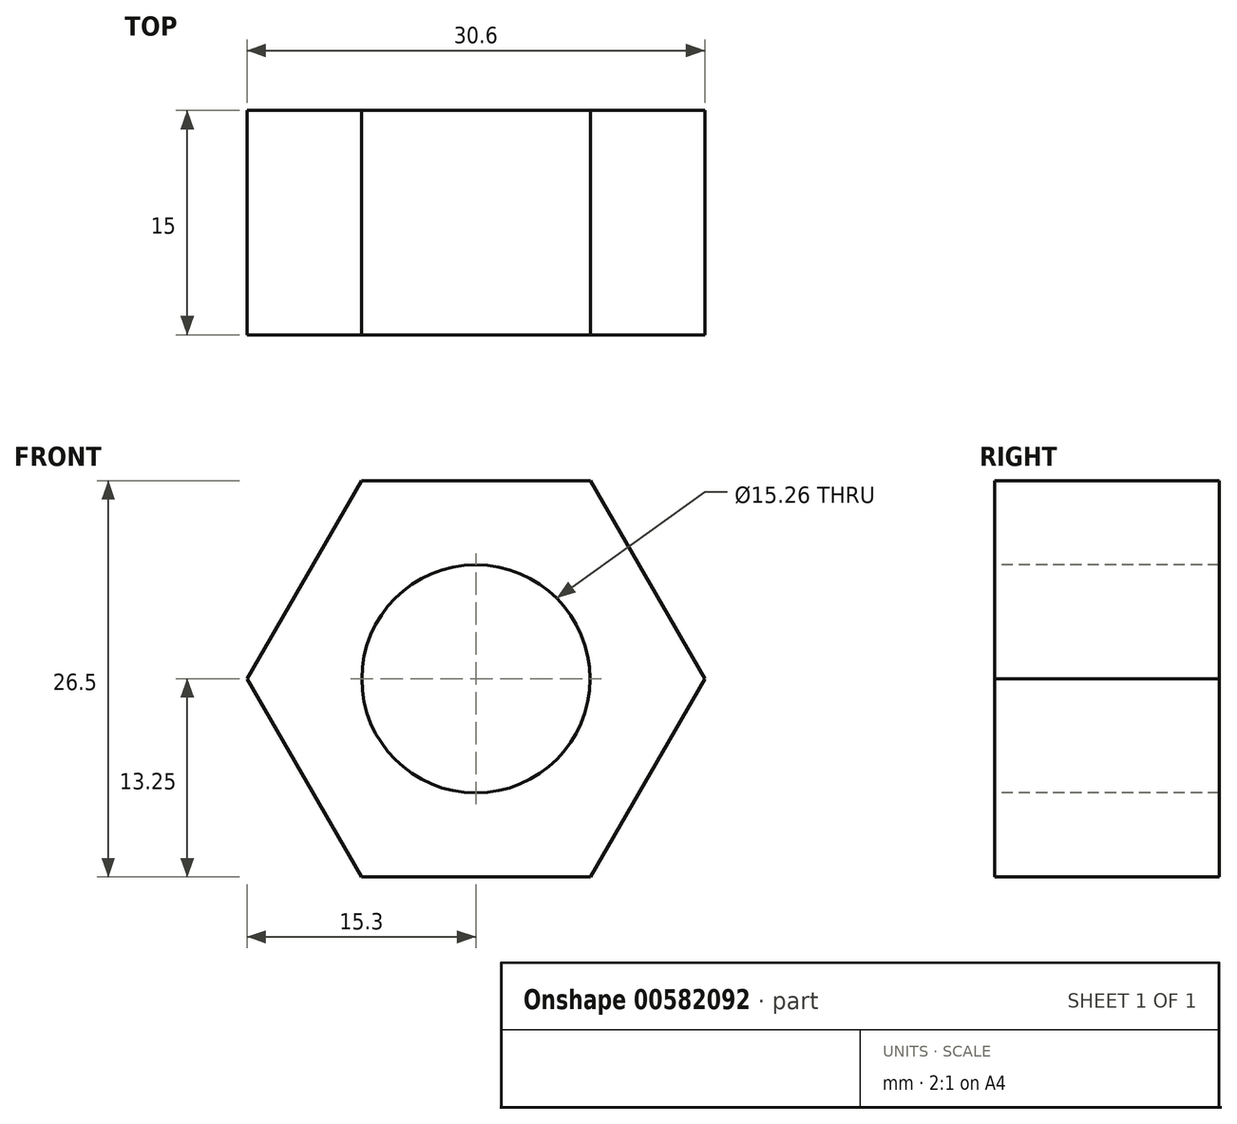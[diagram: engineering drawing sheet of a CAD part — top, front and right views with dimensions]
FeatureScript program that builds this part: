
annotation { "Feature Type Name" : "Feature", "Feature Type Description" : "" }
export const myFeature = defineFeature(function(context is Context, id is Id, definition is map)
    precondition{}
    {
        {
            var Q0;
            Q0=qCreatedBy(makeId("Front.planeOp"),FACE);
            var sketch = newSketch(context, id + "F0", { "sketchPlane" : qUnion([Q0])});
            skCircle(sketch, "E0.cCircle", {"center": v(0, 0) * mm, "radius": 13.25 * mm, "construction": true});
            skLineSegment(sketch, "E0.0", {"start": v(-15.3, 0) * mm, "end": v(-7.65, 13.25) * mm});
            skLineSegment(sketch, "E0.1", {"start": v(-7.65, 13.25) * mm, "end": v(7.65, 13.25) * mm});
            skLineSegment(sketch, "E0.2", {"start": v(7.65, 13.25) * mm, "end": v(15.3, 0) * mm});
            skLineSegment(sketch, "E0.3", {"start": v(15.3, 0) * mm, "end": v(7.65, -13.25) * mm});
            skLineSegment(sketch, "E0.4", {"start": v(7.65, -13.25) * mm, "end": v(-7.65, -13.25) * mm});
            skLineSegment(sketch, "E0.5", {"start": v(-7.65, -13.25) * mm, "end": v(-15.3, 0) * mm});
            skPoint(sketch, "E0.0.midPoint", {"position": v(-11.47, 6.63) * mm});
            skSolve(sketch);
        }
        {
            var Q0;
            Q0 = qSketchRegion(id + "F0", true);
            extrude(context, id + "F1", {"entities" : qUnion([Q0]), "depth" : 15 * mm, "offsetDistance" : 25 * mm});
        }
        {
            var Q0;
            Q0=makeQuery(id+"F1.opExtrude","CAP_FACE",FACE,{"disambiguationData":[OSD([sQuery(id+"F0.wireOp",EDGE,"E0.0"),sQuery(id+"F0.wireOp",EDGE,"E0.1"),sQuery(id+"F0.wireOp",EDGE,"E0.2"),sQuery(id+"F0.wireOp",EDGE,"E0.3"),sQuery(id+"F0.wireOp",EDGE,"E0.4"),sQuery(id+"F0.wireOp",EDGE,"E0.5")])],"isStart":false});
            var sketch = newSketch(context, id + "F2", { "sketchPlane" : qUnion([Q0])});
            skCircle(sketch, "E1", {"center": v(0, 0) * mm, "radius": 7.63 * mm});
            skSolve(sketch);
        }
        {
            var Q0;
            Q0 = qSketchRegion(id + "F2", true);
            extrude(context, id + "F3", {"entities" : qUnion([Q0]), "operationType" : NewBodyOperationType.REMOVE, "endBound" : BoundingType.THROUGH_ALL, "oppositeDirection" : true, "depth" : 25 * mm, "offsetDistance" : 25 * mm});
        }
    });
